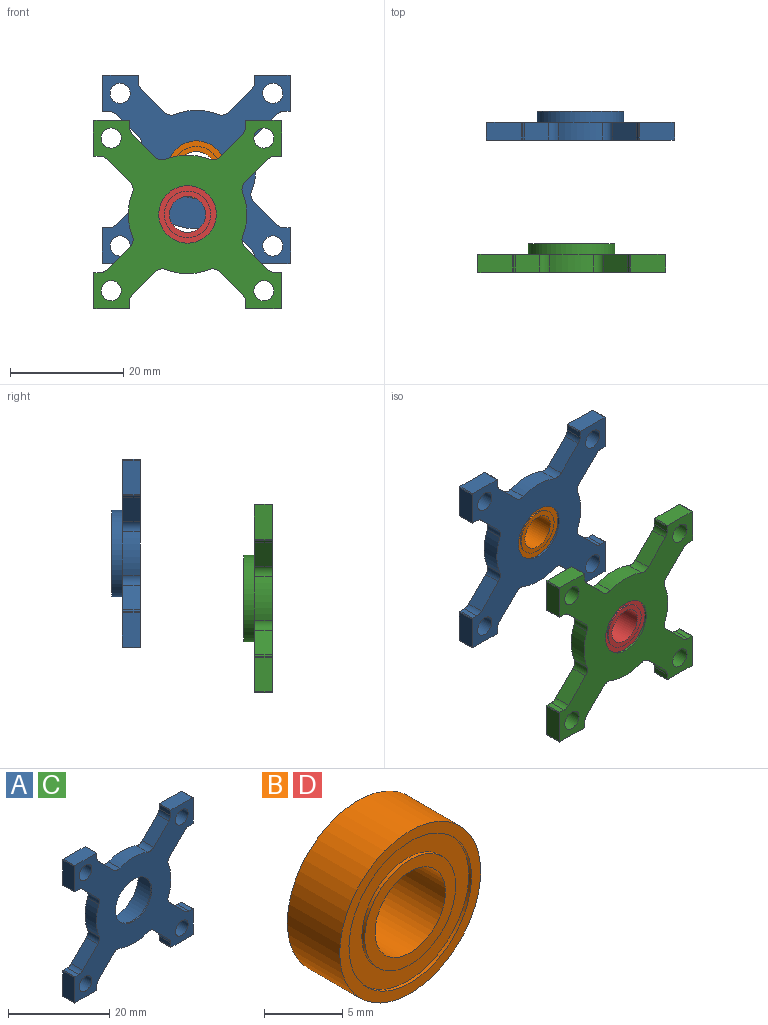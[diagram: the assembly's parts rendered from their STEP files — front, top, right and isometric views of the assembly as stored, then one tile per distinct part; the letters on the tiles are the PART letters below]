
ASSEMBLY  parts=4 mates=1
PART A: 67 faces, bbox 33.3x5.1x33.3 mm
  f0: cylinder r=5.08mm len=10.16mm, axis (0,1,0), area 9.7mm2, adj f38,f66
  f1: cylinder r=6.35mm len=12.7mm, axis (0,-1,0), area 190.5mm2, adj f65,f66
  f2: cylinder r=7.62mm len=15.24mm, axis (0,-1,0), area 91.2mm2, adj f10,f65
  f3: cylinder r=1.59mm len=3.18mm, axis (0,-1,0), area 5.9mm2, adj f10,f23,f24,f38
  f4: cylinder r=1.59mm len=3.18mm, axis (0,-1,0), area 5.9mm2, adj f10,f22,f23,f38
  f5: cylinder r=1.78mm len=3.56mm, axis (0,1,0), area 35.5mm2, adj f10,f38
  f6: cylinder r=1.78mm len=3.56mm, axis (0,1,0), area 35.5mm2, adj f10,f38
  f7: cylinder r=1.78mm len=3.56mm, axis (0,1,0), area 35.5mm2, adj f10,f38
  f8: cylinder r=1.78mm len=3.56mm, axis (0,1,0), area 35.5mm2, adj f10,f38
  f9: cylinder r=10.46mm len=7.74mm, axis (0,-1,0), area 25.2mm2, adj f10,f38,f61,f62
  f10: plane 33.27x33.27mm, normal (0,1,0), area 433.2mm2, adj f2,f3,f4,f5,f6,f7,f8,f9
  f11: plane 3.18x1.08mm, normal (1,0,0), area 3.4mm2, adj f10,f38,f48,f54
  f12: plane 6.1x3.18mm, normal (0,0,-1), area 19.4mm2, adj f10,f38,f48,f49
  f13: plane 6.1x3.18mm, normal (-1,0,0), area 19.4mm2, adj f10,f38,f49,f50
  f14: plane 3.18x1.08mm, normal (0,0,1), area 3.4mm2, adj f10,f38,f50,f53
  f15: plane 4.24x4.24mm, normal (-0.71,0,0.71), area 19mm2, adj f10,f38,f53,f63
  f16: cylinder r=10.46mm len=7.74mm, axis (0,-1,0), area 25.2mm2, adj f10,f38,f63,f64
  f17: plane 4.24x4.24mm, normal (-0.71,0,-0.71), area 19mm2, adj f10,f38,f52,f64
  f18: plane 3.18x1.08mm, normal (0,0,-1), area 3.4mm2, adj f10,f38,f39,f52
  f19: plane 6.1x3.18mm, normal (-1,0,0), area 19.4mm2, adj f10,f38,f39,f40
  f20: plane 6.1x3.18mm, normal (0,0,1), area 19.4mm2, adj f10,f38,f40,f43
  f21: plane 3.18x1.08mm, normal (1,0,0), area 3.4mm2, adj f10,f38,f43,f51
  f22: plane 4.24x4.24mm, normal (0.71,0,0.71), area 19mm2, adj f4,f10,f38,f51
  f23: cylinder r=10.46mm len=7.74mm, axis (0,-1,0), area 25.2mm2, adj f3,f4,f10,f38
  f24: plane 4.24x4.24mm, normal (-0.71,0,0.71), area 19mm2, adj f3,f10,f38,f58
  f25: plane 3.18x1.08mm, normal (-1,0,0), area 3.4mm2, adj f10,f38,f41,f58
  f26: plane 6.1x3.18mm, normal (0,0,1), area 19.4mm2, adj f10,f38,f41,f44
  f27: plane 6.1x3.18mm, normal (1,0,0), area 19.4mm2, adj f10,f38,f44,f45
  f28: plane 3.18x1.08mm, normal (0,0,-1), area 3.4mm2, adj f10,f38,f45,f57
  f29: plane 4.24x4.24mm, normal (0.71,0,-0.71), area 19mm2, adj f10,f38,f57,f59
  f30: cylinder r=10.46mm len=7.74mm, axis (0,-1,0), area 25.2mm2, adj f10,f38,f59,f60
  f31: plane 4.24x4.24mm, normal (0.71,0,0.71), area 19mm2, adj f10,f38,f56,f60
  f32: plane 3.18x1.08mm, normal (0,0,1), area 3.4mm2, adj f10,f38,f46,f56
  f33: plane 6.1x3.18mm, normal (1,0,0), area 19.4mm2, adj f10,f38,f46,f47
  f34: plane 6.1x3.18mm, normal (0,0,-1), area 19.4mm2, adj f10,f38,f42,f47
  f35: plane 3.18x1.08mm, normal (-1,0,0), area 3.4mm2, adj f10,f38,f42,f55
  f36: plane 4.24x4.24mm, normal (-0.71,0,-0.71), area 19mm2, adj f10,f38,f55,f62
  f37: plane 4.24x4.24mm, normal (0.71,0,-0.71), area 19mm2, adj f10,f38,f54,f61
  f38: plane 33.27x33.27mm, normal (0,-1,0), area 534.6mm2, adj f0,f3,f4,f5,f6,f7,f8,f9
  f39: cylinder r=0.13mm len=3.18mm, axis (0,-1,0), area 0.6mm2, adj f10,f18,f19,f38
  f40: cylinder r=0.13mm len=3.18mm, axis (0,1,0), area 0.6mm2, adj f10,f19,f20,f38
  f41: cylinder r=0.13mm len=3.18mm, axis (0,1,0), area 0.6mm2, adj f10,f25,f26,f38
  f42: cylinder r=0.13mm len=3.18mm, axis (0,1,0), area 0.6mm2, adj f10,f34,f35,f38
  f43: cylinder r=0.13mm len=3.18mm, axis (0,-1,0), area 0.6mm2, adj f10,f20,f21,f38
  f44: cylinder r=0.13mm len=3.18mm, axis (0,-1,0), area 0.6mm2, adj f10,f26,f27,f38
  f45: cylinder r=0.13mm len=3.18mm, axis (0,-1,0), area 0.6mm2, adj f10,f27,f28,f38
  f46: cylinder r=0.13mm len=3.18mm, axis (0,-1,0), area 0.6mm2, adj f10,f32,f33,f38
  f47: cylinder r=0.13mm len=3.18mm, axis (0,-1,0), area 0.6mm2, adj f10,f33,f34,f38
  f48: cylinder r=0.13mm len=3.18mm, axis (0,-1,0), area 0.6mm2, adj f10,f11,f12,f38
  f49: cylinder r=0.13mm len=3.18mm, axis (0,-1,0), area 0.6mm2, adj f10,f12,f13,f38
  f50: cylinder r=0.13mm len=3.18mm, axis (0,1,0), area 0.6mm2, adj f10,f13,f14,f38
  f51: cylinder r=1.59mm len=3.18mm, axis (0,-1,0), area 4mm2, adj f10,f21,f22,f38
  f52: cylinder r=1.59mm len=3.18mm, axis (0,-1,0), area 4mm2, adj f10,f17,f18,f38
  f53: cylinder r=1.59mm len=3.18mm, axis (0,-1,0), area 4mm2, adj f10,f14,f15,f38
  f54: cylinder r=1.59mm len=3.18mm, axis (0,-1,0), area 4mm2, adj f10,f11,f37,f38
  f55: cylinder r=1.59mm len=3.18mm, axis (0,-1,0), area 4mm2, adj f10,f35,f36,f38
  f56: cylinder r=1.59mm len=3.18mm, axis (0,-1,0), area 4mm2, adj f10,f31,f32,f38
  f57: cylinder r=1.59mm len=3.18mm, axis (0,-1,0), area 4mm2, adj f10,f28,f29,f38
  f58: cylinder r=1.59mm len=3.18mm, axis (0,-1,0), area 4mm2, adj f10,f24,f25,f38
  f59: cylinder r=1.59mm len=3.18mm, axis (0,-1,0), area 5.9mm2, adj f10,f29,f30,f38
  f60: cylinder r=1.59mm len=3.18mm, axis (0,-1,0), area 5.9mm2, adj f10,f30,f31,f38
  f61: cylinder r=1.59mm len=3.18mm, axis (0,-1,0), area 5.9mm2, adj f9,f10,f37,f38
  f62: cylinder r=1.59mm len=3.18mm, axis (0,-1,0), area 5.9mm2, adj f9,f10,f36,f38
  f63: cylinder r=1.59mm len=3.18mm, axis (0,-1,0), area 5.9mm2, adj f10,f15,f16,f38
  f64: cylinder r=1.59mm len=3.18mm, axis (0,-1,0), area 5.9mm2, adj f10,f16,f17,f38
  f65: plane 15.24x15.24mm, normal (0,1,0), area 55.7mm2, adj f1,f2
  f66: plane 12.7x12.7mm, normal (0,1,0), area 45.6mm2, adj f0,f1
PART B: 12 faces, bbox 12.7x4.7x12.7 mm
  f0: cylinder r=4.1mm len=8.2mm, axis (0,-1,0), area 6.5mm2, adj f6,f11
  f1: cylinder r=5.52mm len=11.05mm, axis (0,-1,0), area 8.8mm2, adj f9,f11
  f2: cylinder r=4.1mm len=8.2mm, axis (0,1,0), area 6.5mm2, adj f7,f10
  f3: cylinder r=5.52mm len=11.05mm, axis (0,1,0), area 8.8mm2, adj f8,f10
  f4: cylinder r=3.17mm len=6.35mm, axis (0,-1,0), area 94.2mm2, adj f6,f7
  f5: cylinder r=6.35mm len=12.7mm, axis (0,-1,0), area 188.5mm2, adj f8,f9
  f6: plane 8.2x8.2mm, normal (0,-1,0), area 21.2mm2, adj f0,f4
  f7: plane 8.2x8.2mm, normal (0,1,0), area 21.2mm2, adj f2,f4
  f8: plane 12.7x12.7mm, normal (0,1,0), area 30.8mm2, adj f3,f5
  f9: plane 12.7x12.7mm, normal (0,-1,0), area 30.8mm2, adj f1,f5
  f10: plane 11.05x11.05mm, normal (0,1,0), area 43mm2, adj f2,f3
  f11: plane 11.05x11.05mm, normal (0,-1,0), area 43mm2, adj f0,f1
PART C: same geometry as A
PART D: same geometry as B
PLACE A t=(6.63,15.25,28.31)mm
PLACE B rot(axis=(0,1,0),34.9deg) t=(6.63,15.55,28.31)mm
PLACE C t=(5.05,-8.04,20.41)mm
PLACE D rot(axis=(0,1,0),0deg) t=(5.05,-7.74,20.41)mm
MATE fastened D.f0 <-> C.f0  axis (0,1,0) through (5.05,-7.74,20.41)mm
